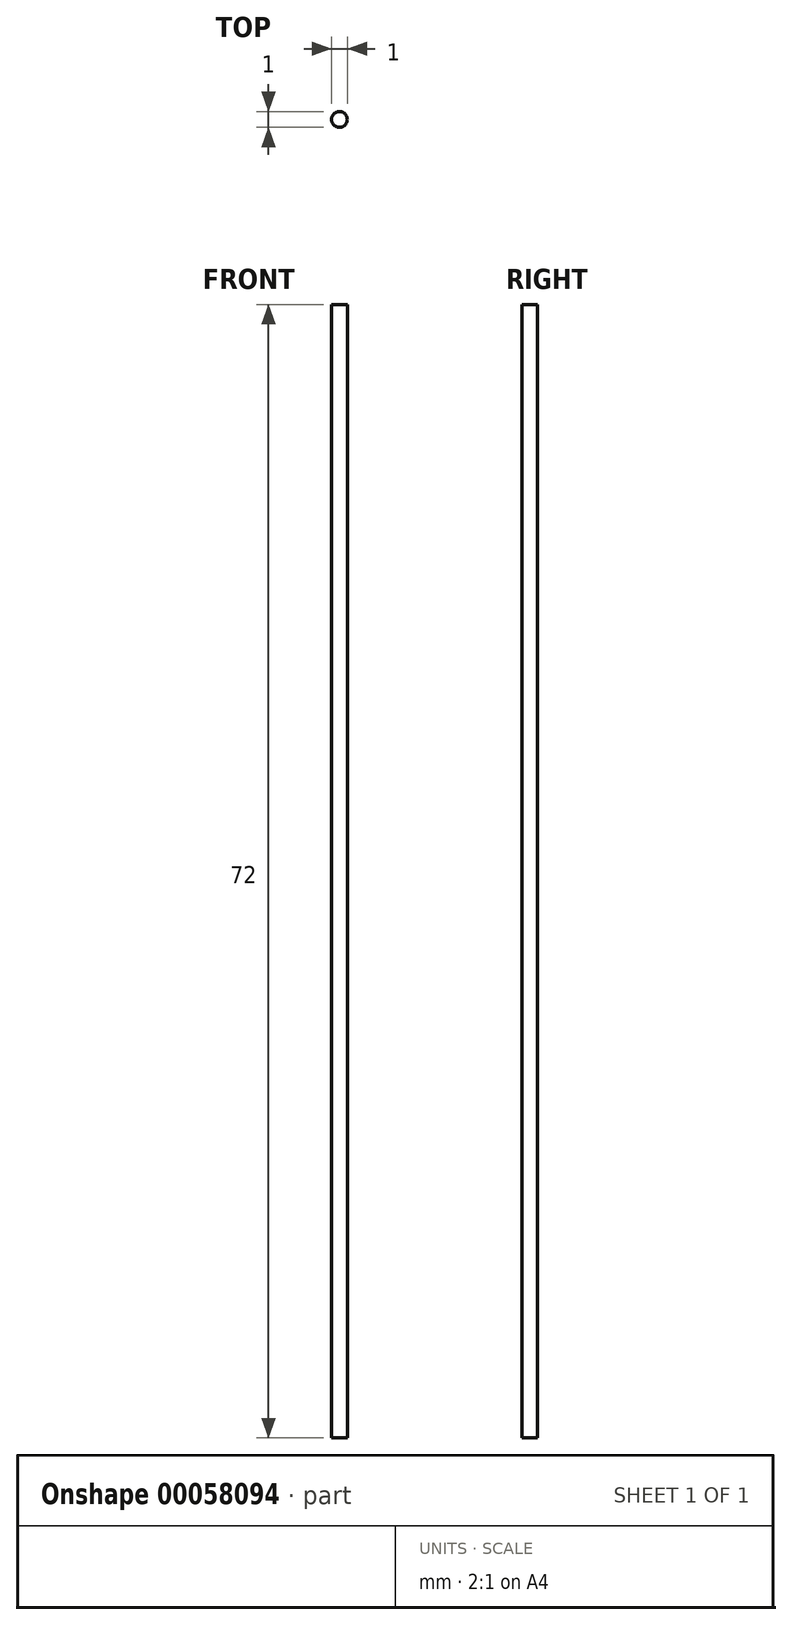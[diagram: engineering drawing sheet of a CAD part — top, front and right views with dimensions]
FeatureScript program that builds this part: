
annotation { "Feature Type Name" : "Feature", "Feature Type Description" : "" }
export const myFeature = defineFeature(function(context is Context, id is Id, definition is map)
    precondition{}
    {
        {
            var Q0;
            Q0=qCreatedBy(makeId("Top.planeOp"),FACE);
            var sketch = newSketch(context, id + "F0", { "sketchPlane" : qUnion([Q0])});
            skCircle(sketch, "E0", {"center": v(0, 0) * mm, "radius": 0.5 * mm});
            skSolve(sketch);
        }
        {
            var Q0;
            Q0 = qSketchRegion(id + "F0", true);
            extrude(context, id + "F1", {"entities" : qUnion([Q0]), "depth" : 72 * mm});
        }
    });
